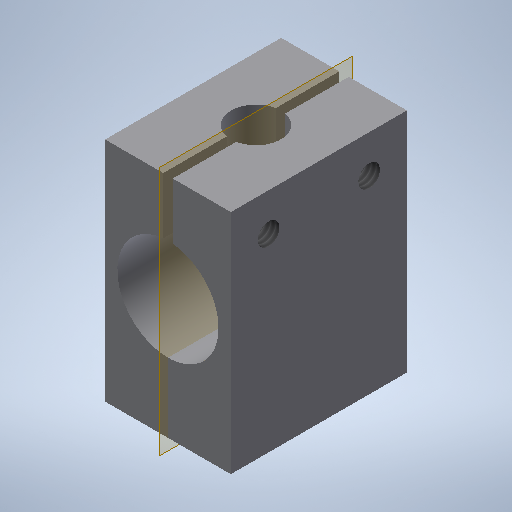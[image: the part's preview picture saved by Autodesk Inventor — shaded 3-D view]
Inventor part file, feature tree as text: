
AUTODESK INVENTOR PART (.ipt)
format: ipt  version: 2025.2 (Build 292293000, 293)  size: 333,824 bytes
history: native  units: mm
features: extrude x9, sketch x4, thread x2, hole x1, plane x1
ambient origin geometry x8: Origin, YZ Plane, XZ Plane, XY Plane, X Axis, Y Axis, Z Axis, Center Point
bodies: Solid1 (feature_tree)
feature tree (17):
  extrude  "Extrusion1"  Depth=36.1mm
  extrude  "Extrusion2"  Depth=10.0mm
  extrude  "Extrusion3"  Depth=19.1mm
  extrude  "Extrusion4"  Depth=29.622mm
  extrude  "Extrusion5"  Depth=29.622mm
  extrude  "Extrusion8"  Depth=29.622mm
  thread  "Thread8"  [1 undecoded]
  thread  "Thread11"  [1 undecoded]
  hole  "Hole1"  [1 undecoded]
  extrude  "Extrusion12"  Depth=29.622mm
  extrude  "Extrusion13"  Depth=10.0mm TaperAngle=0.0deg
  extrude  "Extrusion14"  Depth=29.622mm
  plane  "Work Plane1"
  sketch  "Sketch1"  dims[d0=20.0mm d1=36.1mm]
  sketch  "Sketch3"  dims[d2=28.0mm d3=0.0mm d4=10.0mm]
  sketch  "Sketch11"  dims[d5=16.1mm d6=19.1mm]
  sketch  "Sketch13"  dims[d7=30.0mm d8=0.0mm d9=18.0mm d11=1.5mm d12=0.75mm d13=30.0mm d14=0.0mm d15=14.0mm d16=10.0mm d17=4.572mm d18=10.0mm d19=0.0mm d20=6.0mm d21=6.0mm d22=4.98mm d23=4.98mm d24=6.0mm d25=6.0mm d26=10.0mm d27=0.0mm d28=3.45mm d29=3.45mm d34=10.0mm d35=0.0mm d61=10.0mm d62=0.0mm d67=10.0mm d68=0.0mm d69=5.0mm d71=2.02184mm d74=2.02184mm d75=6.0mm d76=4.0mm d77=2.0mm d78=90.0deg d79=1.91mm d80=20.594885mm d81=0.5mm d82=2.02184mm d83=1.91mm d84=0.0mm d88=6.0mm d89=6.0mm d91=6.0mm d92=6.0mm d93=7.9375mm d94=7.9375mm d95=4.572mm d96=0.0mm d97=10.0mm d98=7.9375mm d99=29.622mm d100=0.0mm d85=0.375mm]
note: 3 required parameter values undecoded (feature->parameter linkage not recoverable at this tier; creation-order binding heuristic only, values carry confidence <= 0.55)
